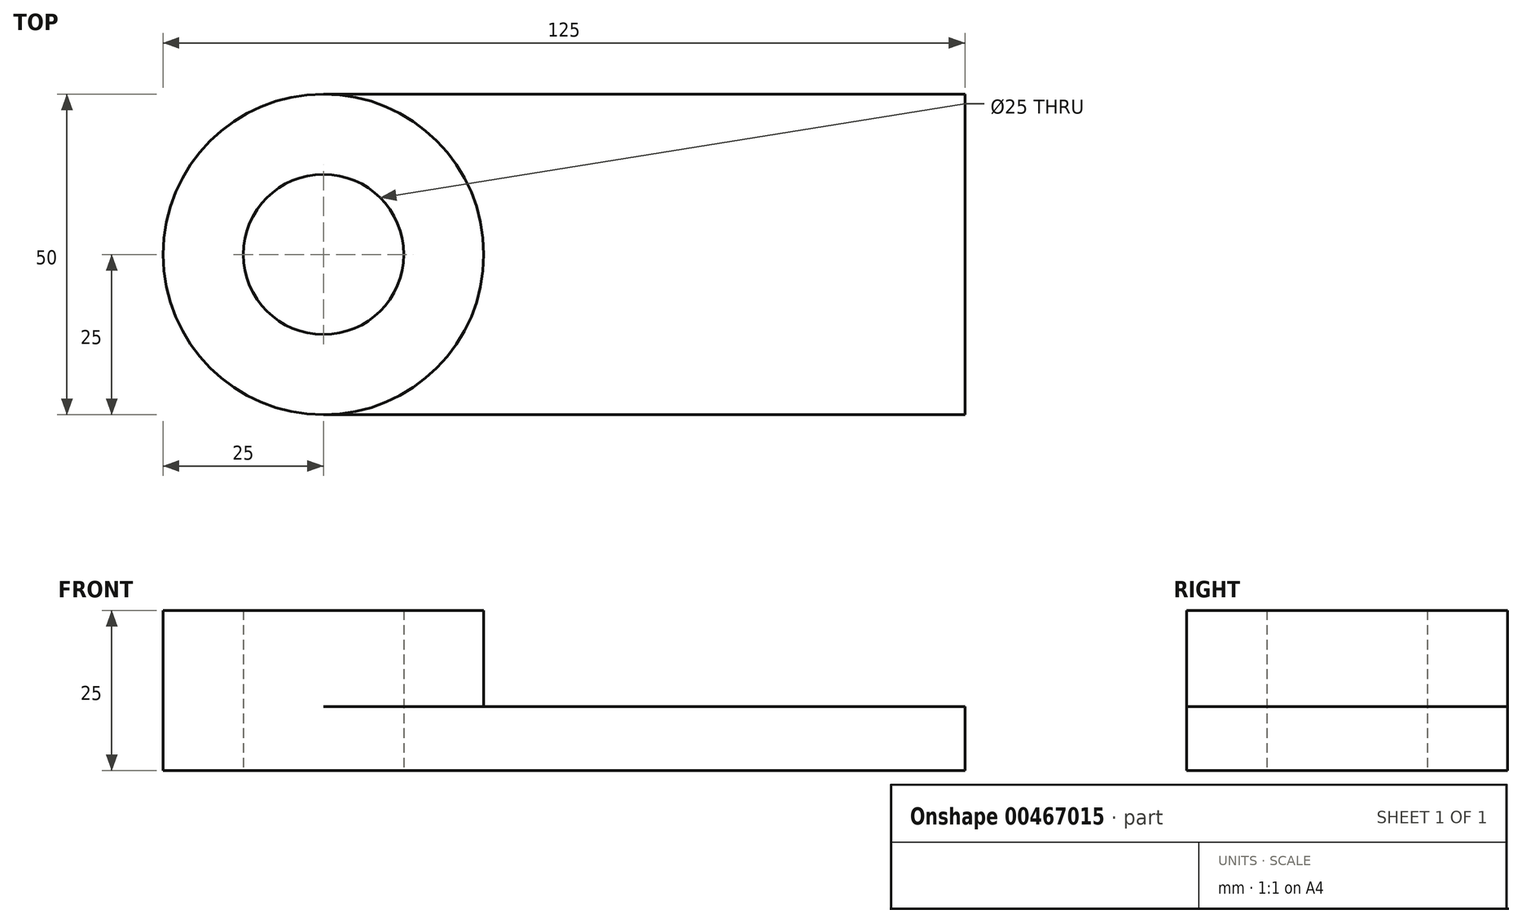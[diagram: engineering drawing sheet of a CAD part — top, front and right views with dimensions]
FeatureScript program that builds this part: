
annotation { "Feature Type Name" : "Feature", "Feature Type Description" : "" }
export const myFeature = defineFeature(function(context is Context, id is Id, definition is map)
    precondition{}
    {
        {
            var Q0;
            Q0=qCreatedBy(makeId("Top.planeOp"),FACE);
            var sketch = newSketch(context, id + "F0", { "sketchPlane" : qUnion([Q0])});
            skLineSegment(sketch, "E0.bottom", {"start": v(50, 25) * mm, "end": v(-50, 25) * mm});
            skLineSegment(sketch, "E0.top", {"start": v(50, -25) * mm, "end": v(-50, -25) * mm});
            skLineSegment(sketch, "E0.left", {"start": v(50, 25) * mm, "end": v(50, -25) * mm});
            skLineSegment(sketch, "E0.right", {"start": v(-50, 25) * mm, "end": v(-50, -25) * mm});
            skPoint(sketch, "E0.middle", {"position": v(0, 0) * mm});
            skCircle(sketch, "E1", {"center": v(-50, 0) * mm, "radius": 25 * mm});
            skCircle(sketch, "E2", {"center": v(-50, 0) * mm, "radius": 12.5 * mm});
            skSolve(sketch);
        }
        {
            var Q0;
            Q0 = qSketchRegion(id + "F0", true);
            var Q1;
            {var subQ0=sQuery(id+"F0.wireOp",EDGE,"E0.bottom");Q1=makeQuery(id+"F0.imprint","IMPRINT",FACE,{"disambiguationData":[TD([[makeQuery(id+"F0.imprint","IMPRINT",EDGE,{"derivedFrom":subQ0}),1.0]])]});}
            extrude(context, id + "F1", {"entities" : qUnion([Q0, Q1]), "depth" : 10 * mm});
        }
        {
            var Q0;
            {var subQ1=sQuery(id+"F0.wireOp",EDGE,"E0.right");var subQ3=sQuery(id+"F0.wireOp",EDGE,"E2");var subQ4=makeQuery(id+"F0.imprint","INTERSECT",VERTEX,{"disambiguationData":[OD(0.0)],"derivedFrom":[subQ1,subQ3]});Q0=makeQuery(id+"F0.imprint","IMPRINT",FACE,{"disambiguationData":[TD([[makeQuery(id+"F0.imprint","IMPRINT",EDGE,{"disambiguationData":[TD([[subQ4,1.0]])],"derivedFrom":subQ3}),-1.0]])]});}
            var sketch = newSketch(context, id + "F2", { "sketchPlane" : qUnion([Q0])});
            skSolve(sketch);
        }
        {
            var Q0;
            Q0 = qSketchRegion(id + "F2", true);
            var Q1;
            {var subQ1=sQuery(id+"F0.wireOp",EDGE,"E0.right");var subQ3=sQuery(id+"F0.wireOp",EDGE,"E2");var subQ4=makeQuery(id+"F0.imprint","INTERSECT",VERTEX,{"disambiguationData":[OD(0.0)],"derivedFrom":[subQ1,subQ3]});Q1=makeQuery(id+"F0.imprint","IMPRINT",FACE,{"disambiguationData":[TD([[makeQuery(id+"F0.imprint","IMPRINT",EDGE,{"disambiguationData":[TD([[subQ4,-1.0]])],"derivedFrom":subQ3}),-1.0]])]});}
            var Q2;
            {var subQ1=sQuery(id+"F0.wireOp",EDGE,"E0.right");var subQ3=sQuery(id+"F0.wireOp",EDGE,"E2");var subQ4=makeQuery(id+"F0.imprint","INTERSECT",VERTEX,{"disambiguationData":[OD(0.0)],"derivedFrom":[subQ1,subQ3]});Q2=makeQuery(id+"F0.imprint","IMPRINT",FACE,{"disambiguationData":[TD([[makeQuery(id+"F0.imprint","IMPRINT",EDGE,{"disambiguationData":[TD([[subQ4,1.0]])],"derivedFrom":subQ3}),-1.0]])]});}
            extrude(context, id + "F3", {"entities" : qUnion([Q0, Q1, Q2]), "operationType" : NewBodyOperationType.ADD, "depth" : 25 * mm});
        }
    });
